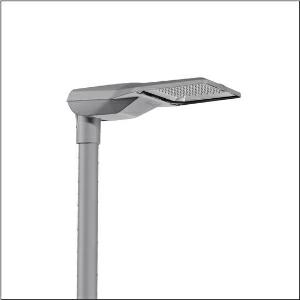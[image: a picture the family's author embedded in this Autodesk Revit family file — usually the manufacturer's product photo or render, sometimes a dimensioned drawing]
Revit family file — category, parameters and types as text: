
# Revit family: streetlight_sl_21_iq_midi___st1_0a_5xe3d61g08nb_ea68
name_source: partatom
category: Lighting Fixtures
units: mm (PartAtom-declared; Revit-internal decimal feet)

## family parameters
Cut with Voids When Loaded = No
Host = Face
Light Source = No
Part Type = Normal
Room Calculation Point = No
Round Connector Dimension = Use Diameter
Shared = No

## types (1)
- --- (1 x LED, 20820 lm, 155.5 W, 2700K)
    Apparent Load = 155 VA
    CIE Flux Codes = 40 73 97 100 100
    Color Rendering = 70
    Color Temperature = 2700K
    Default Elevation = 1800 mm
    Description = Streetlight SL 21 iQ midi, mast luminaire, primary light control with lens, of PMMA, primary optical cover: cover, of toughened safety glass, transparent, light distribution: ST1.0a, light emission: direct distribution, primary light characteristic: asymmetric, installation type: post-top, side-entry, LED, High Power LED, rated luminous flux: 20.820lm, luminous efficacy: 134lm/W, light colour: 727, colour temperature: 2700K, control: Street-Remote, Auto-Match, Temp-Guard, Lumen-Switch, Night-Set, Smart-Wire, Light-Fading, Desk-Remote (wireless, voltage-free reading and setting of iQ features in the workshop via application-optimized NFC function/RFID function), optimised constant luminous flux control (CLO 2.0), pre-setting: linear dimming characteristic, mains connection: 230..240V, AC, 50/60Hz, start of lifetime: 156W, end of service life: 162W, reduction: 69W, luminaire housing, of diecast aluminium, powder-coated, Siteco® metallic grey (DB 702S), corrosivity category C5 mid according to DIN EN ISO 12944, please order mast flange separately, inclination adjustable: 0°, 5°, 10°, 15°, sealing non-destructively replaceable, multi-level sealing system, length: 644mm, width: 335mm, height: 110mm, mast flange for spigot size: 42mm (side-entry): 5XC10008XM4, 60/48mm (side-entry/post-top): 5XC10108XM2, 76/60mm (side-entry/post-top): 5XC10108XM1, protection rating (complete): IP66, insulation class (complete): insulation class II (safety insulation), certification: CE, ENEC, ENEC+, VDE, impact resistance: IK09, permissible operating ambient temperature for outdoor applications: -40..+50°C, standard-compliant lighting for roads and squares, packaging unit: 1 piece

Light Distribution: ST1.0a
    Height = 111 mm
    Lamp = 1 x LED
    Lamp Light Flux = 20820 lm
    Lamp Power = 155.5 W
    Lamp count = 1
    Length = 644 mm
    Luminous efficacy = 134 lm/W
    Manufacturer = Siteco
    ModVariant = No
    Model = 5XE3D61G08NB
    Number of Poles = 1
    OnlyDefault = Yes
    Power Factor = 1
    Product Name = Streetlight SL 21 iQ midi | ST1.0a
    Product group = mast luminaire | pylon top
    ProductGroupID = 6100
    Protection Class = Protection class II
    Protection Degree = IP 66
    RLX_Detail_Level = 1
    RLX_Emergency_Light_Flux = 0 lm
    RLX_Emergency_Type = 0
    RLX_Emergency_Type_DB = No
    RlxData = <blob elided: 91253 chars, md5=f88df910>
    Socket = socket
    Standby Power = 0 W
    System Light Flux = 20820 lm
    System Power = 155 W
    Type Comments = factory setting: luminous flux: 100 % | dim-lin: 254 | 823 mA
    Type Image = l_1004298.jpg
    URL = http://relux.com
    VarID = @adj_141457
    Voltage = 0 V
    Weight = 0.00 kg
    Width = 336 mm

## geometry (parser evidence)
native form markers: Blend x4, Sweep x12
no freeform markers — native parametric forms only
